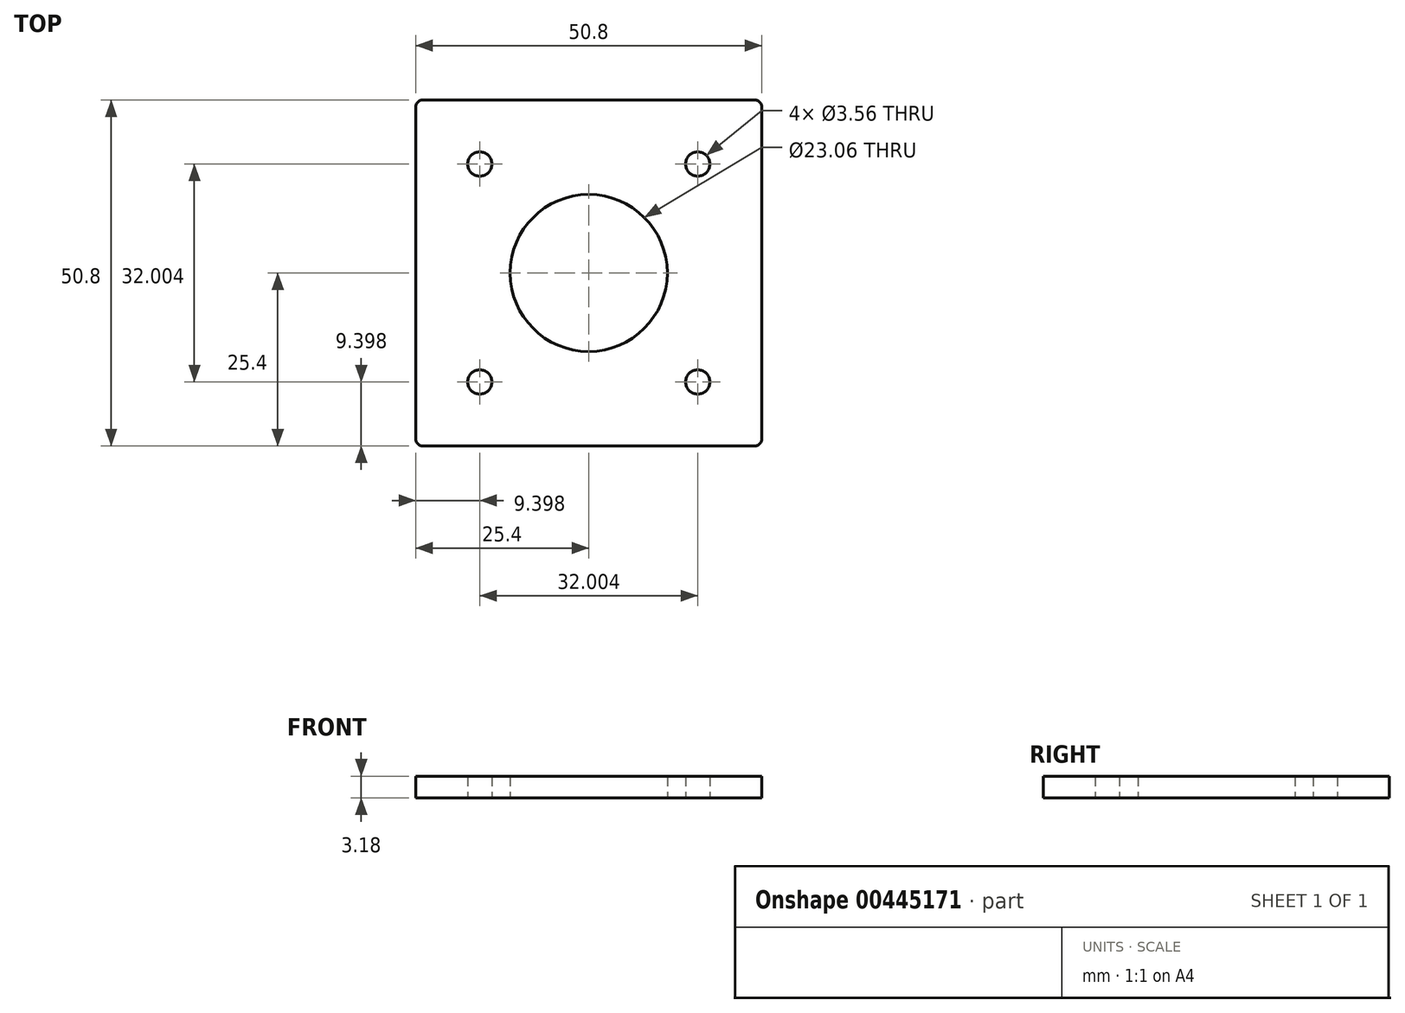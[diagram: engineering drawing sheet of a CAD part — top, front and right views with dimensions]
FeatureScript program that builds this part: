
annotation { "Feature Type Name" : "Feature", "Feature Type Description" : "" }
export const myFeature = defineFeature(function(context is Context, id is Id, definition is map)
    precondition{}
    {
        {
            var Q0;
            Q0=qCreatedBy(makeId("Top.planeOp"),FACE);
            var sketch = newSketch(context, id + "F0", { "sketchPlane" : qUnion([Q0])});
            skLineSegment(sketch, "E0.bottom", {"start": v(50.8, 50.8) * mm, "end": v(0, 50.8) * mm});
            skLineSegment(sketch, "E0.top", {"start": v(50.8, 0) * mm, "end": v(0, 0) * mm});
            skLineSegment(sketch, "E0.left", {"start": v(50.8, 50.8) * mm, "end": v(50.8, 0) * mm});
            skLineSegment(sketch, "E0.right", {"start": v(0, 50.8) * mm, "end": v(0, 0) * mm});
            skCircle(sketch, "E1", {"center": v(25.4, 25.4) * mm, "radius": 11.53 * mm});
            skPoint(sketch, "E1.centerSnap0", {"position": v(50.8, 25.4) * mm});
            skPoint(sketch, "E1.centerSnap1", {"position": v(25.4, 50.8) * mm});
            skLineSegment(sketch, "E2", {"start": v(25.4, 25.4) * mm, "end": v(41.4, 25.4) * mm, "construction": true});
            skLineSegment(sketch, "E3", {"start": v(41.4, 25.4) * mm, "end": v(41.4, 41.4) * mm, "construction": true});
            skCircle(sketch, "E4", {"center": v(41.4, 41.4) * mm, "radius": 1.78 * mm});
            skCircle(sketch, "E5.1.0", {"center": v(9.4, 41.4) * mm, "radius": 1.78 * mm});
            skCircle(sketch, "E5.2.0", {"center": v(9.4, 9.4) * mm, "radius": 1.78 * mm});
            skCircle(sketch, "E5.3.0", {"center": v(41.4, 9.4) * mm, "radius": 1.78 * mm});
            skSolve(sketch);
        }
        {
            var Q0;
            Q0=makeQuery(id+"F0.imprint","IMPRINT",FACE,{"disambiguationData":[TD([[makeQuery(id+"F0.imprint","IMPRINT",EDGE,{"derivedFrom":sQuery(id+"F0.wireOp",EDGE,"E0.bottom")}),1.0]])]});
            extrude(context, id + "F1", {"entities" : qUnion([Q0]), "depth" : 3.17 * mm});
        }
        {
            var Q0;
            Q0=makeQuery(id+"F1.opExtrude","SWEPT_EDGE",EDGE,{"disambiguationData":[OSD([sQuery(id+"F0.wireOp",EDGE,"E0.top"),sQuery(id+"F0.wireOp",EDGE,"E0.left")])]});
            var Q1;
            Q1=makeQuery(id+"F1.opExtrude","SWEPT_EDGE",EDGE,{"disambiguationData":[OSD([sQuery(id+"F0.wireOp",EDGE,"E0.bottom"),sQuery(id+"F0.wireOp",EDGE,"E0.left")])]});
            var Q2;
            Q2=makeQuery(id+"F1.opExtrude","SWEPT_EDGE",EDGE,{"disambiguationData":[OSD([sQuery(id+"F0.wireOp",EDGE,"E0.bottom"),sQuery(id+"F0.wireOp",EDGE,"E0.right")])]});
            var Q3;
            Q3=makeQuery(id+"F1.opExtrude","SWEPT_EDGE",EDGE,{"disambiguationData":[OSD([sQuery(id+"F0.wireOp",EDGE,"E0.top"),sQuery(id+"F0.wireOp",EDGE,"E0.right")])]});
            fillet(context, id + "F2", {"entities" : qUnion([Q0, Q1, Q2, Q3]), "radius" : 1 * mm, "allowEdgeOverflow" : false});
        }
    });
